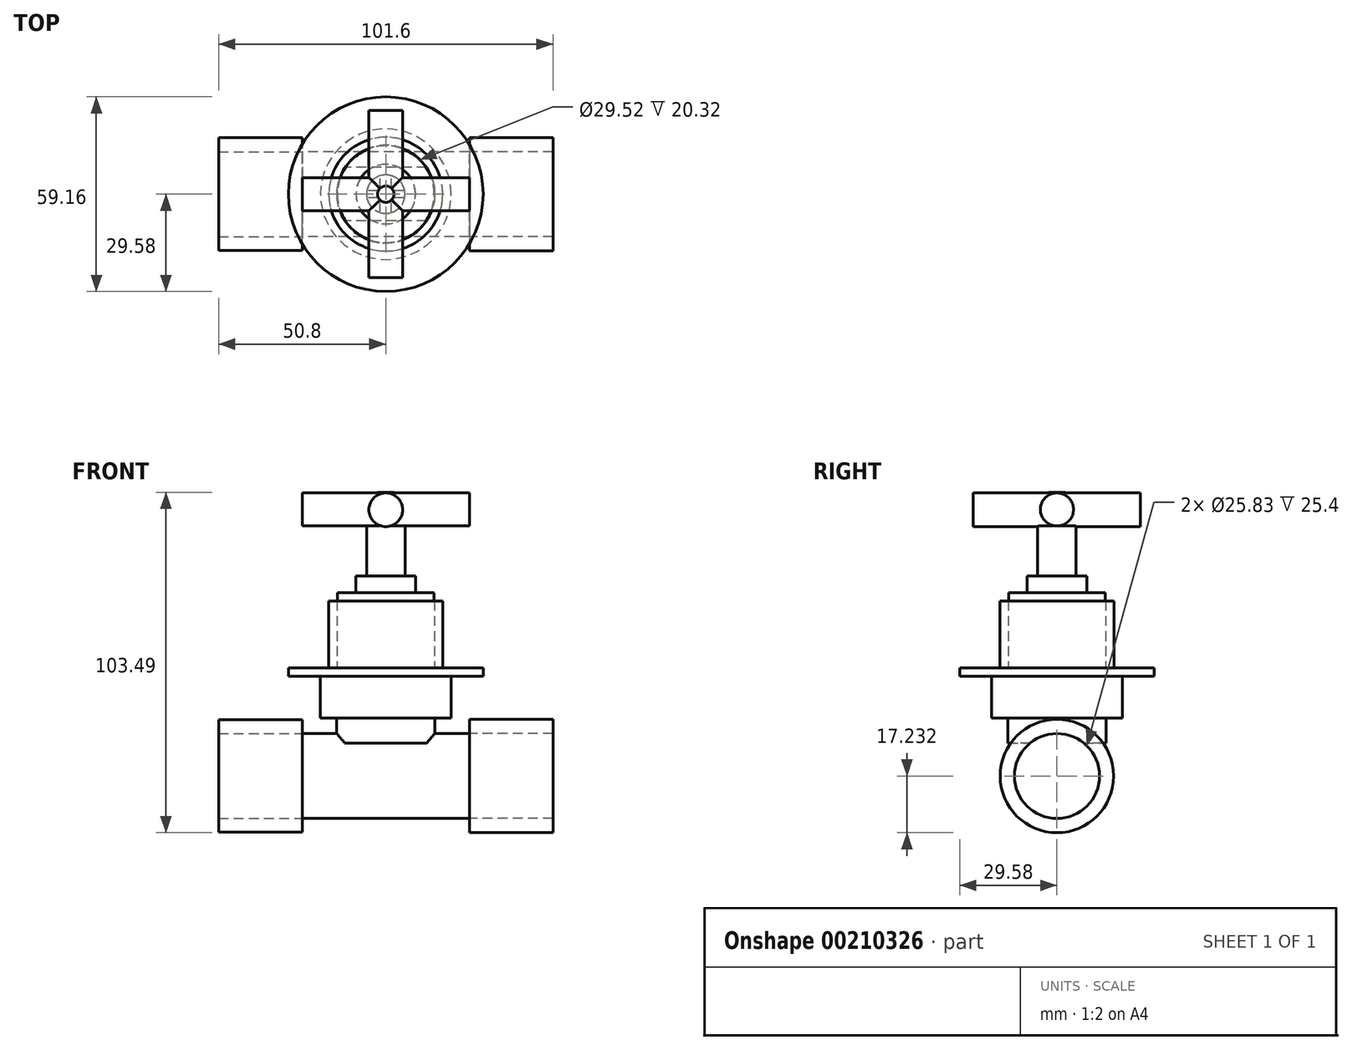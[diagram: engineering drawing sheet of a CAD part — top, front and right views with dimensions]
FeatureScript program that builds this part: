
annotation { "Feature Type Name" : "Feature", "Feature Type Description" : "" }
export const myFeature = defineFeature(function(context is Context, id is Id, definition is map)
    precondition{}
    {
        {
            var Q0;
            Q0=qCreatedBy(makeId("Top.planeOp"),FACE);
            var sketch = newSketch(context, id + "F0", { "sketchPlane" : qUnion([Q0])});
            skCircle(sketch, "E0", {"center": v(0, 0) * mm, "radius": 29.58 * mm});
            skSolve(sketch);
        }
        {
            var Q0;
            Q0=makeQuery(id+"F0.imprint","IMPRINT",FACE,{"disambiguationData":[TD([[makeQuery(id+"F0.imprint","IMPRINT",EDGE,{"derivedFrom":sQuery(id+"F0.wireOp",EDGE,"E0")}),1.0]])]});
            extrude(context, id + "F1", {"entities" : qUnion([Q0]), "depth" : 2.54 * mm});
        }
        {
            var Q0;
            Q0=makeQuery(id+"F1.opExtrude","CAP_FACE",FACE,{"disambiguationData":[OSD([sQuery(id+"F0.wireOp",EDGE,"E0")])],"isStart":false});
            var sketch = newSketch(context, id + "F2", { "sketchPlane" : qUnion([Q0])});
            skCircle(sketch, "E1", {"center": v(0, 0) * mm, "radius": 17.3 * mm});
            skSolve(sketch);
        }
        {
            var Q0;
            Q0=makeQuery(id+"F2.imprint","IMPRINT",FACE,{"disambiguationData":[TD([[makeQuery(id+"F2.imprint","IMPRINT",EDGE,{"derivedFrom":sQuery(id+"F2.wireOp",EDGE,"E1")}),1.0]])]});
            extrude(context, id + "F3", {"entities" : qUnion([Q0]), "operationType" : NewBodyOperationType.ADD, "depth" : 20.32 * mm});
        }
        {
            var Q0;
            Q0=makeQuery(id+"F3.opExtrude","CAP_FACE",FACE,{"disambiguationData":[OSD([sQuery(id+"F2.wireOp",EDGE,"E1")])],"isStart":false});
            shell(context, id + "F4", {"entities" : qUnion([Q0]), "thickness" : 2.54 * mm});
        }
        {
            var Q0;
            Q0=makeQuery(id+"F3.opExtrude","CAP_FACE",FACE,{"disambiguationData":[OSD([sQuery(id+"F2.wireOp",EDGE,"E1")])],"isStart":false});
            var sketch = newSketch(context, id + "F5", { "sketchPlane" : qUnion([Q0])});
            skCircle(sketch, "E2", {"center": v(0, 0) * mm, "radius": 14.7 * mm});
            skSolve(sketch);
        }
        {
            var Q0;
            Q0=makeQuery(id+"F5.imprint","IMPRINT",FACE,{"disambiguationData":[TD([[makeQuery(id+"F5.imprint","IMPRINT",EDGE,{"derivedFrom":sQuery(id+"F5.wireOp",EDGE,"E2")}),1.0]])]});
            extrude(context, id + "F6", {"entities" : qUnion([Q0]), "depth" : 2.54 * mm});
        }
        {
            var Q0;
            Q0=makeQuery(id+"F6.opExtrude","CAP_FACE",FACE,{"disambiguationData":[OSD([sQuery(id+"F5.wireOp",EDGE,"E2")])],"isStart":false});
            var sketch = newSketch(context, id + "F7", { "sketchPlane" : qUnion([Q0])});
            skCircle(sketch, "E3", {"center": v(0, 0) * mm, "radius": 9.03 * mm});
            skSolve(sketch);
        }
        {
            var Q0;
            Q0=makeQuery(id+"F7.imprint","IMPRINT",FACE,{"disambiguationData":[TD([[makeQuery(id+"F7.imprint","IMPRINT",EDGE,{"derivedFrom":sQuery(id+"F7.wireOp",EDGE,"E3")}),1.0]])]});
            extrude(context, id + "F8", {"entities" : qUnion([Q0]), "operationType" : NewBodyOperationType.ADD, "depth" : 5.08 * mm});
        }
        {
            var Q0;
            Q0=makeQuery(id+"F8.opExtrude","CAP_FACE",FACE,{"disambiguationData":[OSD([sQuery(id+"F7.wireOp",EDGE,"E3")])],"isStart":false});
            var sketch = newSketch(context, id + "F9", { "sketchPlane" : qUnion([Q0])});
            skCircle(sketch, "E4", {"center": v(0, 0) * mm, "radius": 5.84 * mm});
            skSolve(sketch);
        }
        {
            var Q0;
            Q0=makeQuery(id+"F9.imprint","IMPRINT",FACE,{"disambiguationData":[TD([[makeQuery(id+"F9.imprint","IMPRINT",EDGE,{"derivedFrom":sQuery(id+"F9.wireOp",EDGE,"E4")}),1.0]])]});
            extrude(context, id + "F10", {"entities" : qUnion([Q0]), "operationType" : NewBodyOperationType.ADD, "depth" : 15.24 * mm});
        }
        {
            var Q0;
            Q0=makeQuery(id+"F10.opExtrude","CAP_FACE",FACE,{"disambiguationData":[OSD([sQuery(id+"F9.wireOp",EDGE,"E4")])],"isStart":false});
            var sketch = newSketch(context, id + "F11", { "sketchPlane" : qUnion([Q0])});
            skCircle(sketch, "E5", {"center": v(0, 0) * mm, "radius": 2.5 * mm});
            skSolve(sketch);
        }
        {
            var Q0;
            Q0=makeQuery(id+"F11.imprint","IMPRINT",FACE,{"disambiguationData":[TD([[makeQuery(id+"F11.imprint","IMPRINT",EDGE,{"derivedFrom":sQuery(id+"F11.wireOp",EDGE,"E5")}),1.0]])]});
            extrude(context, id + "F12", {"entities" : qUnion([Q0]), "operationType" : NewBodyOperationType.ADD, "depth" : 10.16 * mm});
        }
        {
            var Q0;
            Q0=qCreatedBy(makeId("Right.planeOp"),FACE);
            var sketch = newSketch(context, id + "F13", { "sketchPlane" : qUnion([Q0])});
            skCircle(sketch, "E6", {"center": v(0, 50.63) * mm, "radius": 5.03 * mm});
            skSolve(sketch);
        }
        {
            var Q0;
            Q0=makeQuery(id+"F13.imprint","IMPRINT",FACE,{"disambiguationData":[TD([[makeQuery(id+"F13.imprint","IMPRINT",EDGE,{"derivedFrom":sQuery(id+"F13.wireOp",EDGE,"E6")}),1.0]])]});
            extrude(context, id + "F14", {"entities" : qUnion([Q0]), "operationType" : NewBodyOperationType.ADD, "depth" : 25.4 * mm, "hasSecondDirection" : true, "secondDirectionOppositeDirection" : true, "secondDirectionDepth" : 25.4 * mm});
        }
        {
            var Q0;
            Q0=qCreatedBy(makeId("Front.planeOp"),FACE);
            var sketch = newSketch(context, id + "F15", { "sketchPlane" : qUnion([Q0])});
            skCircle(sketch, "E7", {"center": v(0, 50.53) * mm, "radius": 5.12 * mm});
            skSolve(sketch);
        }
        {
            var Q0;
            Q0=makeQuery(id+"F15.imprint","IMPRINT",FACE,{"disambiguationData":[TD([[makeQuery(id+"F15.imprint","IMPRINT",EDGE,{"derivedFrom":sQuery(id+"F15.wireOp",EDGE,"E7")}),1.0]])]});
            extrude(context, id + "F16", {"entities" : qUnion([Q0]), "operationType" : NewBodyOperationType.ADD, "depth" : 25.4 * mm, "hasSecondDirection" : true, "secondDirectionOppositeDirection" : true, "secondDirectionDepth" : 25.4 * mm});
        }
        {
            var Q0;
            Q0=makeQuery(id+"F1.opExtrude","CAP_FACE",FACE,{"disambiguationData":[OSD([sQuery(id+"F0.wireOp",EDGE,"E0")])],"isStart":true});
            var sketch = newSketch(context, id + "F17", { "sketchPlane" : qUnion([Q0])});
            skCircle(sketch, "E8", {"center": v(0, 0) * mm, "radius": 19.84 * mm});
            skSolve(sketch);
        }
        {
            var Q0;
            Q0=makeQuery(id+"F17.imprint","IMPRINT",FACE,{"disambiguationData":[TD([[makeQuery(id+"F17.imprint","IMPRINT",EDGE,{"derivedFrom":sQuery(id+"F17.wireOp",EDGE,"E8")}),1.0]])]});
            extrude(context, id + "F18", {"entities" : qUnion([Q0]), "operationType" : NewBodyOperationType.ADD, "depth" : 12.7 * mm});
        }
        {
            var Q0;
            Q0=makeQuery(id+"F18.opExtrude","CAP_FACE",FACE,{"disambiguationData":[OSD([sQuery(id+"F17.wireOp",EDGE,"E8")])],"isStart":false});
            var sketch = newSketch(context, id + "F19", { "sketchPlane" : qUnion([Q0])});
            skCircle(sketch, "E9", {"center": v(0, 0) * mm, "radius": 14.87 * mm});
            skSolve(sketch);
        }
        {
            var Q0;
            Q0=makeQuery(id+"F19.imprint","IMPRINT",FACE,{"disambiguationData":[TD([[makeQuery(id+"F19.imprint","IMPRINT",EDGE,{"derivedFrom":sQuery(id+"F19.wireOp",EDGE,"E9")}),1.0]])]});
            extrude(context, id + "F20", {"entities" : qUnion([Q0]), "operationType" : NewBodyOperationType.ADD, "depth" : 7.62 * mm});
        }
        {
            var Q0;
            Q0=qCreatedBy(makeId("Right.planeOp"),FACE);
            var sketch = newSketch(context, id + "F21", { "sketchPlane" : qUnion([Q0])});
            skCircle(sketch, "E10", {"center": v(0, -30.38) * mm, "radius": 12.91 * mm});
            skSolve(sketch);
        }
        {
            var Q0;
            Q0=makeQuery(id+"F21.imprint","IMPRINT",FACE,{"disambiguationData":[TD([[makeQuery(id+"F21.imprint","IMPRINT",EDGE,{"derivedFrom":sQuery(id+"F21.wireOp",EDGE,"E10")}),1.0]])]});
            extrude(context, id + "F22", {"entities" : qUnion([Q0]), "operationType" : NewBodyOperationType.ADD, "depth" : 25.4 * mm, "hasSecondDirection" : true, "secondDirectionOppositeDirection" : true, "secondDirectionDepth" : 25.4 * mm});
        }
        {
            var Q0;
            Q0=makeQuery(id+"F22.opExtrude","CAP_FACE",FACE,{"disambiguationData":[OSD([sQuery(id+"F21.wireOp",EDGE,"E10")])],"isStart":true});
            var sketch = newSketch(context, id + "F23", { "sketchPlane" : qUnion([Q0])});
            skCircle(sketch, "E11", {"center": v(0, -30.38) * mm, "radius": 17.12 * mm});
            skSolve(sketch);
        }
        {
            var Q0;
            Q0=makeQuery(id+"F23.imprint","IMPRINT",FACE,{"disambiguationData":[TD([[makeQuery(id+"F23.imprint","IMPRINT",EDGE,{"derivedFrom":sQuery(id+"F23.wireOp",EDGE,"E11")}),1.0]])]});
            extrude(context, id + "F24", {"entities" : qUnion([Q0]), "depth" : 25.4 * mm});
        }
        {
            var Q0;
            Q0=makeQuery(id+"F22.opExtrude","CAP_FACE",FACE,{"disambiguationData":[OSD([sQuery(id+"F21.wireOp",EDGE,"E10")])],"isStart":false});
            var sketch = newSketch(context, id + "F25", { "sketchPlane" : qUnion([Q0])});
            skCircle(sketch, "E12", {"center": v(0, -30.38) * mm, "radius": 17.23 * mm});
            skSolve(sketch);
        }
        {
            var Q0;
            Q0=makeQuery(id+"F25.imprint","IMPRINT",FACE,{"disambiguationData":[TD([[makeQuery(id+"F25.imprint","IMPRINT",EDGE,{"derivedFrom":sQuery(id+"F25.wireOp",EDGE,"E12")}),1.0]])]});
            extrude(context, id + "F26", {"entities" : qUnion([Q0]), "depth" : 25.4 * mm});
        }
    });
